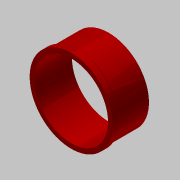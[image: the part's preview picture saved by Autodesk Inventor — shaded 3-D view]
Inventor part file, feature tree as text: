
AUTODESK INVENTOR PART (.ipt)
format: ipt  version: 2017.3 (Build 213257000, 257)  size: 169,984 bytes
history: native  units: in
note: dims shown in document units (in); Inventor stores cm internally (conversion verified against a paired STEP export)
features: extrude x6, sketch x6, chamfer x4, fillet x1, revolve x1
ambient origin geometry x8: Origin, YZ Plane, XZ Plane, XY Plane, X Axis, Y Axis, Z Axis, Center Point
bodies: Solid1 (feature_tree)
feature tree (18):
  extrude  "Extrusion1"  Depth=29.0in
  sketch  "Sketch2"  dims[d2=12.0in d3=0.0in d4=29.23in]
  extrude  "Extrusion2"  Depth=12.0in
  extrude  "Extrusion3"  Depth=1.0in TaperAngle=0.0deg
  chamfer  "Chamfer1"  Distance=1.0in
  extrude  "Extrusion4"  Depth=0.125in TaperAngle=45.0deg
  fillet  "Fillet1"  Radius=27.98in
  chamfer  "Chamfer2"  Distance=0.5in
  chamfer  "Chamfer3"  Distance=0.0312in Angle=45.0deg
  revolve  "Revolution1"  [1 undecoded]
  extrude  "Extrusion5"  Depth=0.125in
  extrude  "Extrusion6"  Depth=0.1875in
  chamfer  "Chamfer6"  Distance=1.25in
  sketch  "Sketch1"  dims[d0=26.5in d1=29.0in]
  sketch  "Sketch3"  dims[d5=29.48in d6=2.0in d7=0.0in d8=1.0in d9=0.0in]
  sketch  "Sketch4"  dims[d10=0.115in d11=0.125in d12=45.0deg d13=27.98in d14=0.5in d15=0.0in]
  sketch  "Sketch5"  dims[d16=0.0312in d17=0.0312in d18=0.125in d19=45.0deg]
  sketch  "Sketch6"  dims[d20=0.0312in d21=0.125in d22=45.0deg d23=0.4375in d24=0.125in d25=0.1875in d26=1.25in d27=45.0deg d28=90.0deg d29=0.5in d30=0.5in d31=0.0in d32=0.0in d33=0.25in d34=0.5in d35=2.0in d36=0.0in d37=0.0in d52=0.375in d53=0.3025in d54=45.0deg]
note: 1 required parameter value undecoded (feature->parameter linkage not recoverable at this tier; creation-order binding heuristic only, values carry confidence <= 0.55)
